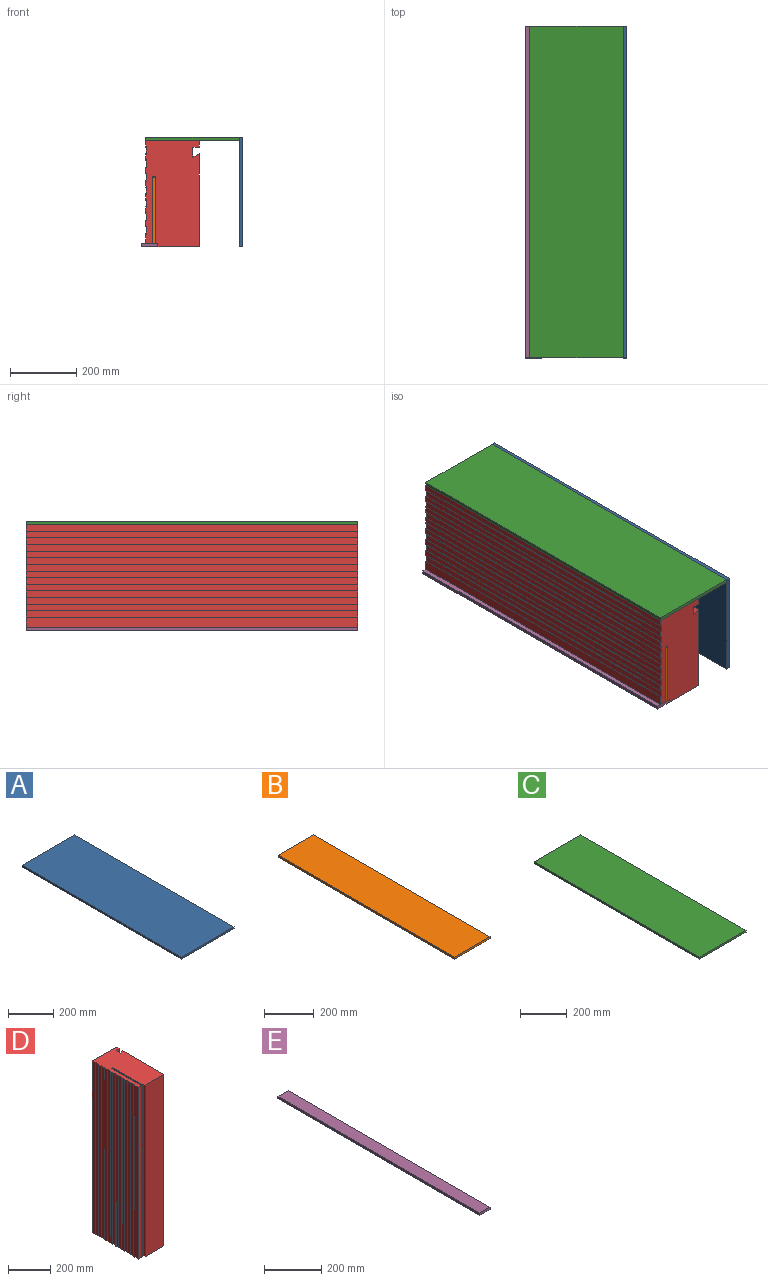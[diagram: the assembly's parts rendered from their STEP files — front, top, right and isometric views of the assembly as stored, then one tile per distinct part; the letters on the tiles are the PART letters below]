
ASSEMBLY  parts=5 mates=4
PART A: 6 faces, bbox 330x1000x10 mm
  f0: plane 1000x10mm, normal (-1,0,0), area 10000mm2, adj f1,f3,f4,f5
  f1: plane 1000x330mm, normal (0,0,-1), area 330000mm2, adj f0,f2,f4,f5
  f2: plane 1000x10mm, normal (1,0,0), area 10000mm2, adj f1,f3,f4,f5
  f3: plane 1000x330mm, normal (0,0,1), area 330000mm2, adj f0,f2,f4,f5
  f4: plane 330x10mm, normal (0,-1,0), area 3300mm2, adj f0,f1,f2,f3
  f5: plane 330x10mm, normal (0,1,0), area 3300mm2, adj f0,f1,f2,f3
PART B: 6 faces, bbox 200x1000x10 mm
  f0: plane 1000x10mm, normal (-1,0,0), area 10000mm2, adj f1,f3,f4,f5
  f1: plane 1000x200mm, normal (0,0,-1), area 200000mm2, adj f0,f2,f4,f5
  f2: plane 1000x10mm, normal (1,0,0), area 10000mm2, adj f1,f3,f4,f5
  f3: plane 1000x200mm, normal (0,0,1), area 200000mm2, adj f0,f2,f4,f5
  f4: plane 200x10mm, normal (0,-1,0), area 2000mm2, adj f0,f1,f2,f3
  f5: plane 200x10mm, normal (0,1,0), area 2000mm2, adj f0,f1,f2,f3
PART C: 6 faces, bbox 282x1000x10 mm
  f0: plane 1000x10mm, normal (-1,0,0), area 10000mm2, adj f1,f3,f4,f5
  f1: plane 1000x282mm, normal (0,0,-1), area 282000mm2, adj f0,f2,f4,f5
  f2: plane 1000x10mm, normal (1,0,0), area 10000mm2, adj f1,f3,f4,f5
  f3: plane 1000x282mm, normal (0,0,1), area 282000mm2, adj f0,f2,f4,f5
  f4: plane 282x10mm, normal (0,-1,0), area 2820mm2, adj f0,f1,f2,f3
  f5: plane 282x10mm, normal (0,1,0), area 2820mm2, adj f0,f1,f2,f3
PART D: 44 faces, bbox 162x320x1000 mm
  f0: plane 1000x20mm, normal (-1,0,0), area 20000mm2, adj f9,f21,f22,f42
  f1: plane 1000x20mm, normal (-1,0,0), area 20000mm2, adj f21,f22,f39,f41
  f2: plane 1000x20mm, normal (-1,0,0), area 20000mm2, adj f21,f22,f36,f38
  f3: plane 1000x20mm, normal (-1,0,0), area 20000mm2, adj f21,f22,f33,f35
  f4: plane 1000x20mm, normal (-1,0,0), area 20000mm2, adj f21,f22,f30,f32
  f5: plane 1000x20mm, normal (-1,0,0), area 20000mm2, adj f21,f22,f27,f29
  f6: plane 1000x20mm, normal (-1,0,0), area 20000mm2, adj f21,f22,f24,f26
  f7: plane 1000x20mm, normal (0,-1,0), area 20000mm2, adj f8,f20,f21,f22
  f8: plane 1000x20mm, normal (1,0,0), area 20000mm2, adj f7,f9,f21,f22
  f9: plane 1000x162mm, normal (0,1,0), area 162000mm2, adj f0,f8,f21,f22
  f10: plane 1000x30mm, normal (-1,0,0), area 30000mm2, adj f11,f21,f22,f23
  f11: plane 1000x20.5mm, normal (0,-1,0), area 20500mm2, adj f10,f12,f21,f22
  f12: plane 1000x202mm, normal (1,0,0), area 202000mm2, adj f11,f13,f21,f22
  f13: cylinder r=10mm len=1000mm, axis (0,0,-1), area 11054.3mm2, adj f12,f14,f21,f22
  f14: plane 1000x202mm, normal (-1,0,0), area 202000mm2, adj f13,f15,f21,f22
  f15: plane 1000x6mm, normal (0,-1,0), area 6000mm2, adj f14,f16,f21,f22
  f16: plane 1000x10mm, normal (-1,0,0), area 10000mm2, adj f15,f17,f21,f22
  f17: plane 1000x125mm, normal (0,-1,0), area 125000mm2, adj f16,f18,f21,f22
  f18: plane 1000x280.19mm, normal (1,0,0), area 280190.5mm2, adj f17,f19,f21,f22
  f19: plane 1000x20mm, normal (-0.45,0.89,0), area 22446.5mm2, adj f18,f20,f21,f22
  f20: plane 1000x30mm, normal (1,0,0), area 30000mm2, adj f7,f19,f21,f22
  f21: plane 320x162mm, normal (0,0,1), area 48553.5mm2, adj f0,f1,f2,f3,f4,f5,f6,f7
  f22: plane 320x162mm, normal (0,0,-1), area 48553.5mm2, adj f0,f1,f2,f3,f4,f5,f6,f7
  f23: plane 1000x2mm, normal (0.71,0.71,0), area 2828.4mm2, adj f10,f21,f22,f25
  f24: plane 1000x2mm, normal (0.71,-0.71,0), area 2828.4mm2, adj f6,f21,f22,f25
  f25: plane 1000x24mm, normal (-1,0,0), area 24000mm2, adj f21,f22,f23,f24
  f26: plane 1000x2mm, normal (0.71,0.71,0), area 2828.4mm2, adj f6,f21,f22,f28
  f27: plane 1000x2mm, normal (0.71,-0.71,0), area 2828.4mm2, adj f5,f21,f22,f28
  f28: plane 1000x24mm, normal (-1,0,0), area 24000mm2, adj f21,f22,f26,f27
  f29: plane 1000x2mm, normal (0.71,0.71,0), area 2828.4mm2, adj f5,f21,f22,f31
  f30: plane 1000x2mm, normal (0.71,-0.71,0), area 2828.4mm2, adj f4,f21,f22,f31
  f31: plane 1000x24mm, normal (-1,0,0), area 24000mm2, adj f21,f22,f29,f30
  f32: plane 1000x2mm, normal (0.71,0.71,0), area 2828.4mm2, adj f4,f21,f22,f34
  f33: plane 1000x2mm, normal (0.71,-0.71,0), area 2828.4mm2, adj f3,f21,f22,f34
  f34: plane 1000x24mm, normal (-1,0,0), area 24000mm2, adj f21,f22,f32,f33
  f35: plane 1000x2mm, normal (0.71,0.71,0), area 2828.4mm2, adj f3,f21,f22,f37
  f36: plane 1000x2mm, normal (0.71,-0.71,0), area 2828.4mm2, adj f2,f21,f22,f37
  f37: plane 1000x24mm, normal (-1,0,0), area 24000mm2, adj f21,f22,f35,f36
  f38: plane 1000x2mm, normal (0.71,0.71,0), area 2828.4mm2, adj f2,f21,f22,f40
  f39: plane 1000x2mm, normal (0.71,-0.71,0), area 2828.4mm2, adj f1,f21,f22,f40
  f40: plane 1000x24mm, normal (-1,0,0), area 24000mm2, adj f21,f22,f38,f39
  f41: plane 1000x2mm, normal (0.71,0.71,0), area 2828.4mm2, adj f1,f21,f22,f43
  f42: plane 1000x2mm, normal (0.71,-0.71,0), area 2828.4mm2, adj f0,f21,f22,f43
  f43: plane 1000x24mm, normal (-1,0,0), area 24000mm2, adj f21,f22,f41,f42
PART E: 6 faces, bbox 50x1000x10 mm
  f0: plane 1000x10mm, normal (-1,0,0), area 10000mm2, adj f1,f3,f4,f5
  f1: plane 1000x50mm, normal (0,0,-1), area 50000mm2, adj f0,f2,f4,f5
  f2: plane 1000x10mm, normal (1,0,0), area 10000mm2, adj f1,f3,f4,f5
  f3: plane 1000x50mm, normal (0,0,1), area 50000mm2, adj f0,f2,f4,f5
  f4: plane 50x10mm, normal (0,-1,0), area 500mm2, adj f0,f1,f2,f3
  f5: plane 50x10mm, normal (0,1,0), area 500mm2, adj f0,f1,f2,f3
PLACE A rot(axis=(0,1,0),90deg) t=(91.17,500,65.28)mm
PLACE B rot(axis=(0,1,0),90deg) t=(-170.08,500,-54.72)mm
PLACE C t=(-190.83,500,55.28)mm fixed
PLACE D rot(axis=(1,0,0),90deg) t=(-17.59,500,-54.89)mm
PLACE E t=(-203.83,500,-264.72)mm
MATE fastened A.f1 <-> C.f2  axis (-1,0,0) through (91.17,-500,65.28)mm
MATE fastened B.f4 <-> D.f21  axis (0,-1,0) through (-159.83,-500,-52.72)mm
MATE fastened C.f1 <-> D.f9  axis (0,0,-1) through (-190.83,-500,55.28)mm
MATE fastened E.f4 <-> D.f21  axis (0,-1,0) through (-153.83,-500,-254.72)mm
